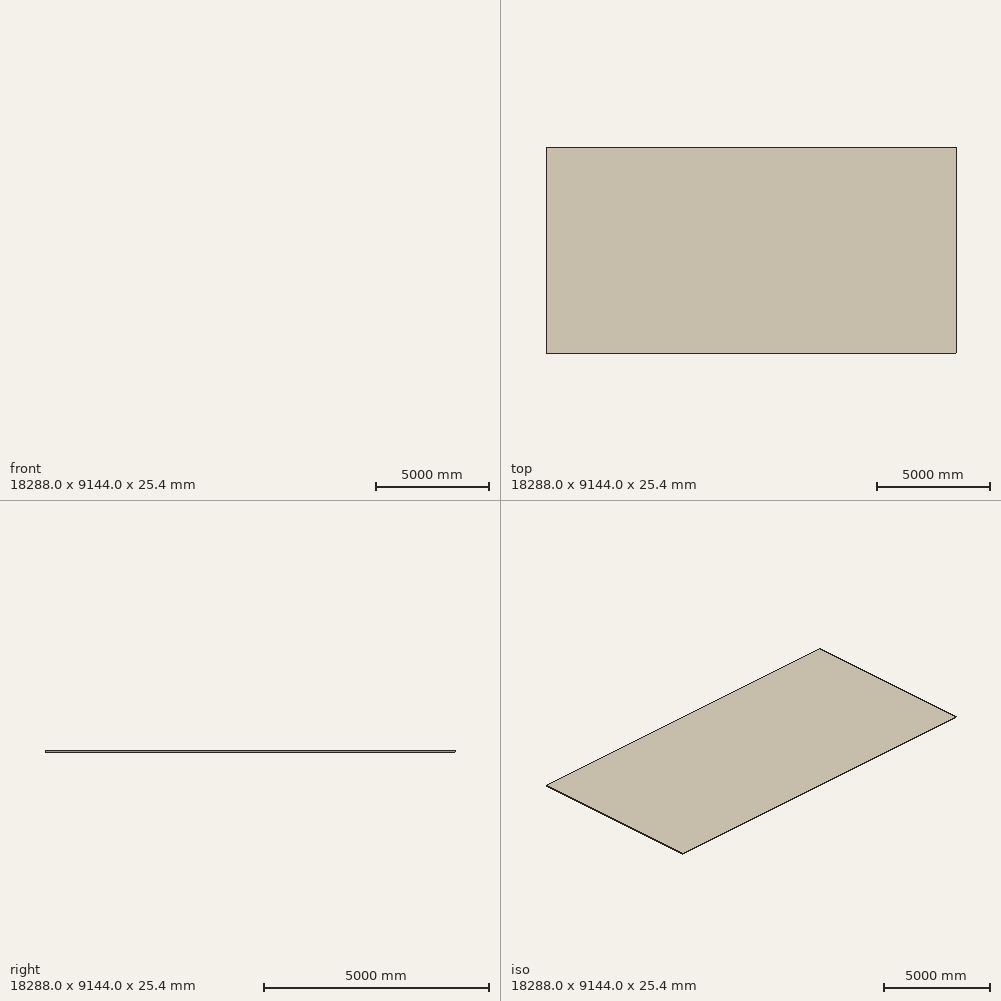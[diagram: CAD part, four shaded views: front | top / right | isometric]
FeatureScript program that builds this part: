
annotation { "Feature Type Name" : "Feature", "Feature Type Description" : "" }
export const myFeature = defineFeature(function(context is Context, id is Id, definition is map)
    precondition{}
    {
        {
            var Q0;
            Q0=qCreatedBy(makeId("Top.planeOp"),FACE);
            var sketch = newSketch(context, id + "F0", { "sketchPlane" : qUnion([Q0])});
            skLineSegment(sketch, "E0.bottom", {"start": v(9144, 4572) * mm, "end": v(-9144, 4572) * mm});
            skLineSegment(sketch, "E0.top", {"start": v(9144, -4572) * mm, "end": v(-9144, -4572) * mm});
            skLineSegment(sketch, "E0.left", {"start": v(9144, 4572) * mm, "end": v(9144, -4572) * mm});
            skLineSegment(sketch, "E0.right", {"start": v(-9144, 4572) * mm, "end": v(-9144, -1828.8) * mm});
            skPoint(sketch, "E0.middle", {"position": v(0, 0) * mm});
            skLineSegment(sketch, "E1.bottom", {"start": v(-9144, 4572) * mm, "end": v(-3048, 4572) * mm});
            skLineSegment(sketch, "E1.top", {"start": v(-9144, -1828.8) * mm, "end": v(-3048, -1828.8) * mm});
            skLineSegment(sketch, "E1.right", {"start": v(-3048, 4572) * mm, "end": v(-3048, -1828.8) * mm});
            skLineSegment(sketch, "E2", {"start": v(-3048, 0) * mm, "end": v(-7010.4, 0) * mm});
            skPoint(sketch, "E2.endSnap0", {"position": v(-9144, 0) * mm});
            skLineSegment(sketch, "E3", {"start": v(-7010.4, 4572) * mm, "end": v(-7010.4, 0) * mm});
            skLineSegment(sketch, "E4.bottom", {"start": v(4876.8, 4572) * mm, "end": v(9144, 4572) * mm});
            skLineSegment(sketch, "E4.top", {"start": v(4876.8, 914.4) * mm, "end": v(9144, 914.4) * mm});
            skLineSegment(sketch, "E4.left", {"start": v(4876.8, 4572) * mm, "end": v(4876.8, 914.4) * mm});
            skLineSegment(sketch, "E4.right", {"start": v(9144, 4572) * mm, "end": v(9144, 914.4) * mm});
            skLineSegment(sketch, "E5.bottom", {"start": v(9144, -4572) * mm, "end": v(4876.8, -4572) * mm});
            skLineSegment(sketch, "E5.top", {"start": v(9144, -914.4) * mm, "end": v(4876.8, -914.4) * mm});
            skLineSegment(sketch, "E5.left", {"start": v(9144, -4572) * mm, "end": v(9144, -914.4) * mm});
            skLineSegment(sketch, "E5.right", {"start": v(4876.8, -4572) * mm, "end": v(4876.8, -914.4) * mm});
            skLineSegment(sketch, "E6", {"start": v(6096, 914.4) * mm, "end": v(6096, -914.4) * mm});
            skLineSegment(sketch, "E7", {"start": v(-5181.6, -1828.8) * mm, "end": v(-5181.6, -4572) * mm});
            skLineSegment(sketch, "E8", {"start": v(-9144, -1828.8) * mm, "end": v(-9144, -4572) * mm});
            skLineSegment(sketch, "E9", {"start": v(-7010.4, 0) * mm, "end": v(-7010.4, -1828.8) * mm});
            skSolve(sketch);
        }
        {
            var Q0;
            Q0=sQuery(id+"F0.wireOp",EDGE,"E0.right");
            var Q1;
            Q1=sQuery(id+"F0.wireOp",EDGE,"E0.top");
            var Q2;
            Q2=sQuery(id+"F0.wireOp",EDGE,"E0.bottom");
            var Q3;
            Q3=sQuery(id+"F0.wireOp",EDGE,"E0.left");
            extrude(context, id + "F1", {"bodyType" : ToolBodyType.SURFACE, "surfaceEntities" : qUnion([Q0, Q1, Q2, Q3]), "depth" : 3048 * mm, "offsetDistance" : 25.4 * mm});
        }
        {
            var Q0;
            Q0=sQuery(id+"F0.wireOp",EDGE,"E3");
            var Q1;
            Q1=sQuery(id+"F0.wireOp",EDGE,"E2");
            var Q2;
            Q2=sQuery(id+"F0.wireOp",EDGE,"E1.top");
            var Q3;
            Q3=sQuery(id+"F0.wireOp",EDGE,"E4.left");
            var Q4;
            Q4=sQuery(id+"F0.wireOp",EDGE,"E4.top");
            var Q5;
            Q5=sQuery(id+"F0.wireOp",EDGE,"E5.top");
            var Q6;
            Q6=sQuery(id+"F0.wireOp",EDGE,"E5.right");
            extrude(context, id + "F2", {"bodyType" : ToolBodyType.SURFACE, "surfaceEntities" : qUnion([Q0, Q1, Q2, Q3, Q4, Q5, Q6]), "depth" : 3048 * mm, "offsetDistance" : 25.4 * mm});
        }
        {
            var Q0;
            Q0=sQuery(id+"F0.wireOp",EDGE,"E1.right");
            var Q1;
            Q1=sQuery(id+"F0.wireOp",EDGE,"E7");
            var Q2;
            Q2=sQuery(id+"F0.wireOp",EDGE,"E6");
            var Q3;
            Q3=sQuery(id+"F0.wireOp",EDGE,"E9");
            extrude(context, id + "F3", {"bodyType" : ToolBodyType.SURFACE, "surfaceEntities" : qUnion([Q0, Q1, Q2, Q3]), "depth" : 3048 * mm, "offsetDistance" : 25.4 * mm});
        }
        {
            var Q0;
            {var subQ2=sQuery(id+"F0.wireOp",EDGE,"E4.left");Q0=makeQuery(id+"F0.imprint","IMPRINT",FACE,{"disambiguationData":[TD([[makeQuery(id+"F0.imprint","IMPRINT",EDGE,{"derivedFrom":subQ2}),-1.0]])]});}
            var Q1;
            {var subQ4=sQuery(id+"F0.wireOp",EDGE,"E2");Q1=makeQuery(id+"F0.imprint","IMPRINT",FACE,{"disambiguationData":[TD([[makeQuery(id+"F0.imprint","IMPRINT",EDGE,{"derivedFrom":subQ4}),-1.0]])]});}
            var Q2;
            {var subQ3=sQuery(id+"F0.wireOp",EDGE,"E2");Q2=makeQuery(id+"F0.imprint","IMPRINT",FACE,{"disambiguationData":[TD([[makeQuery(id+"F0.imprint","IMPRINT",EDGE,{"derivedFrom":subQ3}),1.0]])]});}
            var Q3;
            {var subQ2=sQuery(id+"F0.wireOp",EDGE,"E0.right");Q3=makeQuery(id+"F0.imprint","IMPRINT",FACE,{"disambiguationData":[TD([[makeQuery(id+"F0.imprint","IMPRINT",EDGE,{"derivedFrom":subQ2}),1.0]])]});}
            var Q4;
            {var subQ0=sQuery(id+"F0.wireOp",EDGE,"E7");Q4=makeQuery(id+"F0.imprint","IMPRINT",FACE,{"disambiguationData":[TD([[makeQuery(id+"F0.imprint","IMPRINT",EDGE,{"derivedFrom":subQ0}),-1.0]])]});}
            var Q5;
            {var subQ2=sQuery(id+"F0.wireOp",EDGE,"E4.left");Q5=makeQuery(id+"F0.imprint","IMPRINT",FACE,{"disambiguationData":[TD([[makeQuery(id+"F0.imprint","IMPRINT",EDGE,{"derivedFrom":subQ2}),1.0]])]});}
            var Q6;
            {var subQ5=sQuery(id+"F0.wireOp",EDGE,"E6");Q6=makeQuery(id+"F0.imprint","IMPRINT",FACE,{"disambiguationData":[TD([[makeQuery(id+"F0.imprint","IMPRINT",EDGE,{"derivedFrom":subQ5}),1.0]])]});}
            var Q7;
            {var subQ4=sQuery(id+"F0.wireOp",EDGE,"E5.right");Q7=makeQuery(id+"F0.imprint","IMPRINT",FACE,{"disambiguationData":[TD([[makeQuery(id+"F0.imprint","IMPRINT",EDGE,{"derivedFrom":subQ4}),-1.0]])]});}
            extrude(context, id + "F4", {"entities" : qUnion([Q0, Q1, Q2, Q3, Q4, Q5, Q6, Q7]), "depth" : 25.4 * mm, "offsetDistance" : 25.4 * mm});
        }
    });
